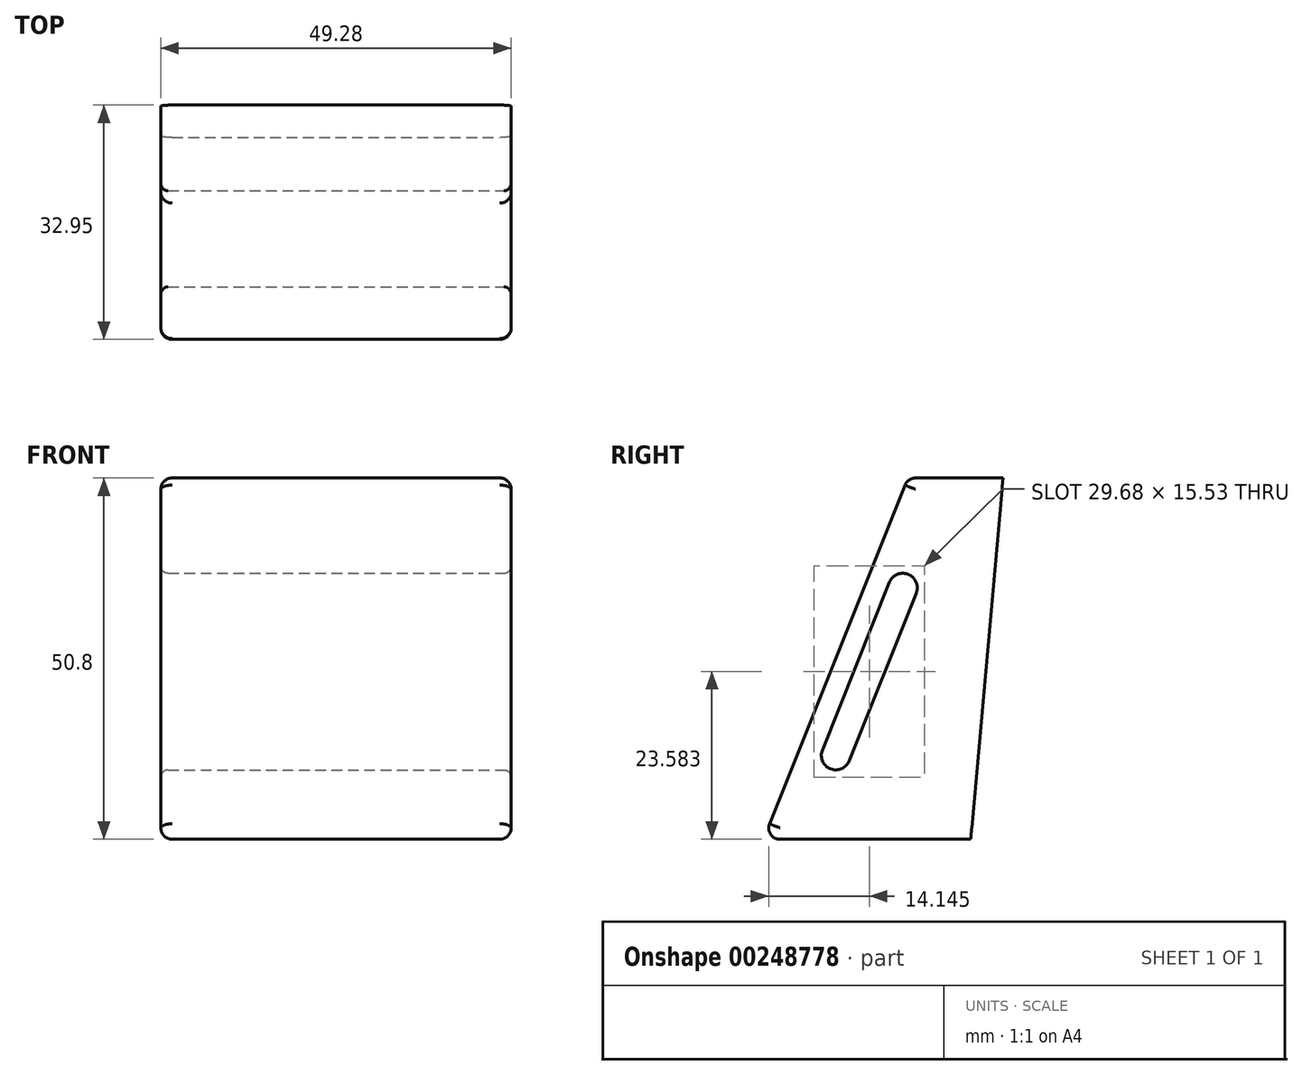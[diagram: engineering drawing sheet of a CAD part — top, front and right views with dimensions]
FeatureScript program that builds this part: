
annotation { "Feature Type Name" : "Feature", "Feature Type Description" : "" }
export const myFeature = defineFeature(function(context is Context, id is Id, definition is map)
    precondition{}
    {
        {
            var Q0;
            Q0=qCreatedBy(makeId("Front.planeOp"),FACE);
            var sketch = newSketch(context, id + "F0", { "sketchPlane" : qUnion([Q0])});
            skLineSegment(sketch, "E0.bottom", {"start": v(24.64, 25.4) * mm, "end": v(-24.64, 25.4) * mm});
            skLineSegment(sketch, "E0.top", {"start": v(24.64, -25.4) * mm, "end": v(-24.64, -25.4) * mm});
            skLineSegment(sketch, "E0.left", {"start": v(24.64, 25.4) * mm, "end": v(24.64, -25.4) * mm});
            skLineSegment(sketch, "E0.right", {"start": v(-24.64, 25.4) * mm, "end": v(-24.64, -25.4) * mm});
            skPoint(sketch, "E0.middle", {"position": v(0, 0) * mm});
            skSolve(sketch);
        }
        {
            var Q0;
            Q0 = qSketchRegion(id + "F0", true);
            extrude(context, id + "F1", {"entities" : qUnion([Q0]), "depth" : 8.5 * mm});
        }
        {
            var Q0;
            Q0=makeQuery(id+"F1.opExtrude","SWEPT_FACE",FACE,{"disambiguationData":[OSD([sQuery(id+"F0.wireOp",EDGE,"E0.left")])]});
            var sketch = newSketch(context, id + "F2", { "sketchPlane" : qUnion([Q0])});
            skLineSegment(sketch, "E1", {"start": v(-8.5, 25.4) * mm, "end": v(-8.5, -25.4) * mm});
            skLineSegment(sketch, "E2", {"start": v(-8.5, -25.4) * mm, "end": v(-41.52, -25.4) * mm});
            skLineSegment(sketch, "E3", {"start": v(-41.52, -25.4) * mm, "end": v(-21.2, 25.4) * mm});
            skLineSegment(sketch, "E4", {"start": v(-21.2, 25.4) * mm, "end": v(-8.5, 25.4) * mm});
            skLineSegment(sketch, "E5", {"start": v(-15.73, 25.4) * mm, "end": v(-36.05, -25.4) * mm, "construction": true});
            skLineSegment(sketch, "E6", {"start": v(-20.01, 9.22) * mm, "end": v(-29.45, -14.36) * mm});
            skLineSegment(sketch, "E7", {"start": v(-23.79, 10.73) * mm, "end": v(-33.22, -12.85) * mm});
            skLineSegment(sketch, "E8", {"start": v(-23.79, 10.73) * mm, "end": v(-20.01, 9.22) * mm, "construction": true});
            skLineSegment(sketch, "E9", {"start": v(-29.45, -14.36) * mm, "end": v(-33.22, -12.85) * mm, "construction": true});
            skArc(sketch, "E10", {"start": v(-20.01, 9.22) * mm, "mid": v(-21.14, 11.86) * mm, "end": v(-23.79, 10.73) * mm});
            skArc(sketch, "E11", {"start": v(-33.22, -12.85) * mm, "mid": v(-32.09, -15.5) * mm, "end": v(-29.45, -14.36) * mm});
            skSolve(sketch);
        }
        {
            var Q0;
            Q0 = qSketchRegion(id + "F2", true);
            var Q1;
            Q1=makeQuery(id+"F1.opExtrude","SWEPT_FACE",FACE,{"disambiguationData":[OSD([sQuery(id+"F0.wireOp",EDGE,"E0.right")])]});
            extrude(context, id + "F3", {"entities" : qUnion([Q0]), "operationType" : NewBodyOperationType.ADD, "endBound" : BoundingType.UP_TO_SURFACE, "oppositeDirection" : true, "endBoundEntityFace" : qUnion([Q1]), "depth" : 25.4 * mm});
        }
        {
            var Q0;
            Q0=makeQuery(id+"F3.opExtrude","SWEPT_FACE",FACE,{"disambiguationData":[OSD([sQuery(id+"F2.wireOp",EDGE,"E3")])]});
            fillet(context, id + "F4", {"entities" : qUnion([Q0]), "radius" : 1.59 * mm, "tangentPropagation" : true, "allowEdgeOverflow" : false});
        }
        {
            var Q0;
            Q0=makeQuery(id+"F3.boolean.opBoolean","MERGE",FACE,{"derivedFrom":[makeQuery(id+"F1.opExtrude","SWEPT_FACE",FACE,{"disambiguationData":[OSD([sQuery(id+"F0.wireOp",EDGE,"E0.bottom")])]}),makeQuery(id+"F3.opExtrude","SWEPT_FACE",FACE,{"disambiguationData":[OSD([sQuery(id+"F2.wireOp",EDGE,"E4")])]})]});
            fillet(context, id + "F5", {"entities" : qUnion([Q0]), "radius" : 1.59 * mm, "tangentPropagation" : true, "allowEdgeOverflow" : false});
        }
        {
            var Q0;
            Q0=makeQuery(id+"F3.boolean.opBoolean","MERGE",FACE,{"derivedFrom":[makeQuery(id+"F1.opExtrude","SWEPT_FACE",FACE,{"disambiguationData":[OSD([sQuery(id+"F0.wireOp",EDGE,"E0.top")])]}),makeQuery(id+"F3.opExtrude","SWEPT_FACE",FACE,{"disambiguationData":[OSD([sQuery(id+"F2.wireOp",EDGE,"E2")])]})]});
            fillet(context, id + "F6", {"entities" : qUnion([Q0]), "radius" : 1.59 * mm, "tangentPropagation" : true, "allowEdgeOverflow" : false});
        }
        {
            var Q0;
            Q0=makeQuery(id+"F3.opExtrude","CAP_EDGE",EDGE,{"disambiguationData":[OSD([sQuery(id+"F2.wireOp",EDGE,"E7")])],"isStart":true});
            fillet(context, id + "F7", {"entities" : qUnion([Q0]), "radius" : 1.02 * mm, "tangentPropagation" : true, "allowEdgeOverflow" : false});
        }
        {
            var Q0;
            Q0=makeQuery(id+"F3.opExtrude","CAP_EDGE",EDGE,{"disambiguationData":[OSD([sQuery(id+"F2.wireOp",EDGE,"E6")])],"isStart":false});
            fillet(context, id + "F8", {"entities" : qUnion([Q0]), "radius" : 1.02 * mm, "tangentPropagation" : true, "allowEdgeOverflow" : false});
        }
        {
            var Q0;
            Q0=makeQuery(id+"F3.boolean.opBoolean","MERGE",FACE,{"derivedFrom":[makeQuery(id+"F1.opExtrude","SWEPT_FACE",FACE,{"disambiguationData":[OSD([sQuery(id+"F0.wireOp",EDGE,"E0.left")])]}),makeQuery(id+"F3.opExtrude","CAP_FACE",FACE,{"disambiguationData":[OSD([sQuery(id+"F2.wireOp",EDGE,"E1"),sQuery(id+"F2.wireOp",EDGE,"E2"),sQuery(id+"F2.wireOp",EDGE,"E3"),sQuery(id+"F2.wireOp",EDGE,"E4"),sQuery(id+"F2.wireOp",EDGE,"E6"),sQuery(id+"F2.wireOp",EDGE,"E7"),sQuery(id+"F2.wireOp",EDGE,"E10"),sQuery(id+"F2.wireOp",EDGE,"E11")])],"isStart":true})]});
            var sketch = newSketch(context, id + "F9", { "sketchPlane" : qUnion([Q0])});
            skLineSegment(sketch, "E12.bottom", {"start": v(7.58, 27.93) * mm, "end": v(-7.62, 27.93) * mm});
            skLineSegment(sketch, "E12.top", {"start": v(7.58, -36.2) * mm, "end": v(-7.62, -36.2) * mm});
            skLineSegment(sketch, "E12.left", {"start": v(7.58, 27.93) * mm, "end": v(7.58, -36.2) * mm});
            skLineSegment(sketch, "E12.right", {"start": v(-7.62, 27.93) * mm, "end": v(-7.62, -36.2) * mm});
            skSolve(sketch);
        }
        {
            var Q0;
            Q0 = qSketchRegion(id + "F9", true);
            extrude(context, id + "F10", {"entities" : qUnion([Q0]), "operationType" : NewBodyOperationType.REMOVE, "endBound" : BoundingType.THROUGH_ALL, "oppositeDirection" : true, "depth" : 25.4 * mm});
        }
        {
            var Q0;
            Q0=makeQuery(id+"F3.boolean.opBoolean","MERGE",FACE,{"derivedFrom":[makeQuery(id+"F1.opExtrude","SWEPT_FACE",FACE,{"disambiguationData":[OSD([sQuery(id+"F0.wireOp",EDGE,"E0.left")])]}),makeQuery(id+"F3.opExtrude","CAP_FACE",FACE,{"disambiguationData":[OSD([sQuery(id+"F2.wireOp",EDGE,"E1"),sQuery(id+"F2.wireOp",EDGE,"E2"),sQuery(id+"F2.wireOp",EDGE,"E3"),sQuery(id+"F2.wireOp",EDGE,"E4"),sQuery(id+"F2.wireOp",EDGE,"E6"),sQuery(id+"F2.wireOp",EDGE,"E7"),sQuery(id+"F2.wireOp",EDGE,"E10"),sQuery(id+"F2.wireOp",EDGE,"E11")])],"isStart":true})]});
            var sketch = newSketch(context, id + "F11", { "sketchPlane" : qUnion([Q0])});
            skLineSegment(sketch, "E13", {"start": v(-7.62, 27.47) * mm, "end": v(-7.62, -25.92) * mm});
            skLineSegment(sketch, "E14", {"start": v(-7.62, -25.92) * mm, "end": v(-12.4, -25.92) * mm});
            skLineSegment(sketch, "E15", {"start": v(-12.4, -25.92) * mm, "end": v(-7.62, 27.47) * mm});
            skSolve(sketch);
        }
        {
            var Q0;
            Q0 = qSketchRegion(id + "F11", true);
            extrude(context, id + "F12", {"entities" : qUnion([Q0]), "operationType" : NewBodyOperationType.REMOVE, "endBound" : BoundingType.THROUGH_ALL, "oppositeDirection" : true, "depth" : 25.4 * mm});
        }
    });
